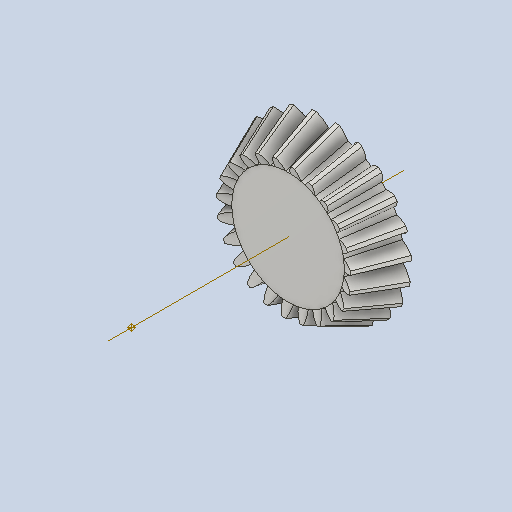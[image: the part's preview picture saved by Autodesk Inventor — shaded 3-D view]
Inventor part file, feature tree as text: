
AUTODESK INVENTOR PART (.ipt)
format: ipt  version: 2023 (Build 270158030, 158C)  size: 559,104 bytes
history: native  units: mm
features: other x24, loft x2, pattern_circular x2, sketch x1
ambient origin geometry x6: Origin, XZ Plane, X Axis, Y Axis, Z Axis, Center Point
bodies: Solid1 (feature_tree)
feature tree (29):
  other  "Top Point"
  other  "Mesh Plane2"
  other  "Teeth Body"
  other  "Start Point"
  other  "Tooth Plane"
  other  "Start Sketch"
  other  "End Point"
  other  "3D Sketch Right"
  other  "End Plane Right"
  loft  "Loft Right"
  pattern_circular  "Circular Pattern Right"  [2 undecoded]
  other  "3D Sketch Left"
  other  "End Plane Left"
  loft  "Loft Left"
  pattern_circular  "Circular Pattern Left"  [2 undecoded]
  other  "Fix Body"
  other  "Mesh Plane"
  other  "Top Plane"
  other  "Teeth Body Sketch"
  other  "End Plane"
  other  "End Sketch"
  other  "Helical Curve Left"
  other  "End Sketch Left"
  other  "Body Sketch"
  sketch  "Sketch6"  dims[d0=69.0mm d1=62.323077mm d2=74.564103mm d3=20.0mm d4=84.377418mm d5=90.0deg d7=13.741113mm d8=14.921461mm d9=31.50969mm d11=20.33mm d12=10.711152mm d15=11.631229mm d16=24.561698mm d17=0.0mm d18=90.0deg d19=0.0mm d20=90.0deg d21=230.0mm d22=360.0deg d26=492.398605mm d27=18.853034mm d28=69.0mm d29=-3.835275mm d30=10.711152mm d31=11.631229mm d32=24.561698mm d35=0.0mm d37=0.0mm d39=0.0mm d40=90.0deg d41=230.0mm d42=360.0deg d46=90.0deg d47=90.0deg d48=0.0mm d49=0.0mm d50=90.0deg d51=1.36591mm d52=0.0mm d53=0.0mm d54=0.0mm d56=27.073959mm d57=42.182765mm d58=32.810765mm d59=32.881325mm d60=25.575882mm d61=32.881325mm d62=25.575882mm d65=492.398605mm d66=31.5mm d67=69.0mm d68=-3.835275mm d69=18.853034mm d70=11.631229mm d71=24.561698mm d72=10.711152mm d73=25.575882mm d74=32.881325mm d75=0.0mm d77=0.0mm d79=0.0mm d80=90.0deg d81=230.0mm d82=360.0deg d84=10.0mm d85=20.0mm d86=20.0mm d87=10.0mm d88=0.0mm d89=0.0mm d90=90.0deg d91=90.0deg d92=90.0deg d93=90.0deg]
  other  "Srf1"
  other  "Helical Curve Right"
  other  "End Sketch Right"
  other  "Pitch Diameter"
note: 4 required parameter values undecoded (feature->parameter linkage not recoverable at this tier; creation-order binding heuristic only, values carry confidence <= 0.55)
